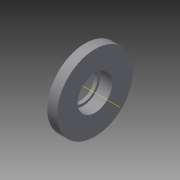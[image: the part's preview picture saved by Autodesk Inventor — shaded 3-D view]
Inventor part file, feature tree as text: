
AUTODESK INVENTOR PART (.ipt)
format: ipt  version: 2014 (Build 180170000, 170)  size: 99,840 bytes
history: native  units: in
note: dims shown in document units (in); Inventor stores cm internally (conversion verified against a paired STEP export)
features: reference x7, sketch x1, other x1, revolve x1
ambient origin geometry x8: Origin, YZ Plane, XZ Plane, XY Plane, X Axis, Y Axis, Z Axis, Center Point
bodies: Solid1 (feature_tree)
feature tree (10):
  sketch  "Sketch1"  dims[d0=0.025in d1=0.025in d2=0.01in d3=0.01in d4=0.01in d5=0.1in d6=0.1in d7=0.075in d8=90.0deg]
  other  "Work Axis1"
  revolve  "Revolution1"  [1 undecoded]
  reference  "Reference1"
  reference  "Reference2"
  reference  "Reference3"
  reference  "Reference4"
  reference  "Reference5"
  reference  "Reference6"
  reference  "Reference7"
note: 1 required parameter value undecoded (feature->parameter linkage not recoverable at this tier; creation-order binding heuristic only, values carry confidence <= 0.55)
